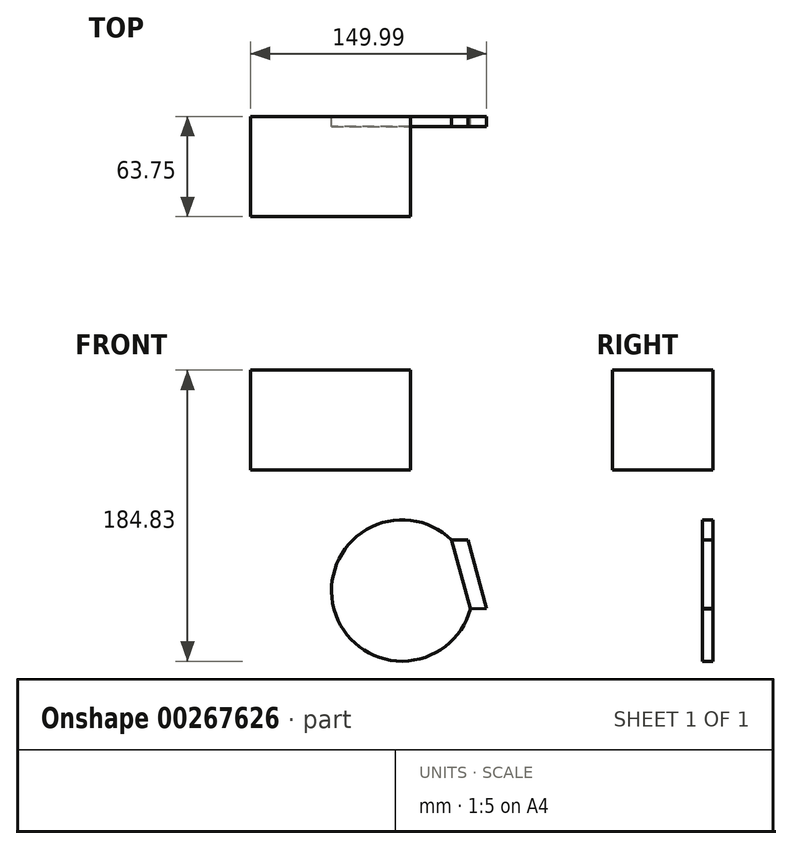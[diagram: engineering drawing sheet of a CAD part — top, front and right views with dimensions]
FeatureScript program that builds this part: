
annotation { "Feature Type Name" : "Feature", "Feature Type Description" : "" }
export const myFeature = defineFeature(function(context is Context, id is Id, definition is map)
    precondition{}
    {
        {
            var Q0;
            Q0=qCreatedBy(makeId("Front.planeOp"),FACE);
            var sketch = newSketch(context, id + "F0", { "sketchPlane" : qUnion([Q0])});
            skLineSegment(sketch, "E0.bottom", {"start": v(12.41, 15.98) * mm, "end": v(-89.19, 15.98) * mm});
            skLineSegment(sketch, "E0.top", {"start": v(12.41, 79.48) * mm, "end": v(-89.19, 79.48) * mm});
            skLineSegment(sketch, "E0.left", {"start": v(12.41, 15.98) * mm, "end": v(12.41, 79.48) * mm});
            skLineSegment(sketch, "E0.right", {"start": v(-89.19, 15.98) * mm, "end": v(-89.19, 79.48) * mm});
            skPoint(sketch, "E0.middle", {"position": v(-38.39, 47.73) * mm});
            skArc(sketch, "E1", {"start": v(38.56, -28.43) * mm, "mid": v(-36.12, -72.34) * mm, "end": v(50.5, -72.03) * mm});
            skLineSegment(sketch, "E2", {"start": v(38.56, -28.43) * mm, "end": v(50.5, -72.03) * mm});
            skLineSegment(sketch, "E3", {"start": v(38.56, -28.43) * mm, "end": v(48.89, -28.43) * mm});
            skLineSegment(sketch, "E4", {"start": v(48.89, -28.43) * mm, "end": v(60.8, -71.9) * mm});
            skLineSegment(sketch, "E5", {"start": v(60.8, -71.9) * mm, "end": v(50.5, -72.03) * mm});
            skSolve(sketch);
        }
        {
            var Q0;
            Q0=makeQuery(id+"F0.imprint","IMPRINT",FACE,{"disambiguationData":[TD([[makeQuery(id+"F0.imprint","IMPRINT",EDGE,{"derivedFrom":sQuery(id+"F0.wireOp",EDGE,"E0.bottom")}),-1.0]])]});
            extrude(context, id + "F1", {"entities" : qUnion([Q0]), "depth" : 63.75 * mm});
        }
        {
            var Q0;
            Q0=makeQuery(id+"F0.imprint","IMPRINT",FACE,{"disambiguationData":[TD([[makeQuery(id+"F0.imprint","IMPRINT",EDGE,{"derivedFrom":sQuery(id+"F0.wireOp",EDGE,"E1")}),1.0]])]});
            extrude(context, id + "F2", {"entities" : qUnion([Q0]), "depth" : 6.6 * mm});
        }
        {
            var Q0;
            Q0=makeQuery(id+"F0.imprint","IMPRINT",FACE,{"disambiguationData":[TD([[makeQuery(id+"F0.imprint","IMPRINT",EDGE,{"derivedFrom":sQuery(id+"F0.wireOp",EDGE,"E2")}),1.0]])]});
            extrude(context, id + "F3", {"entities" : qUnion([Q0]), "depth" : 6.6 * mm});
        }
    });
